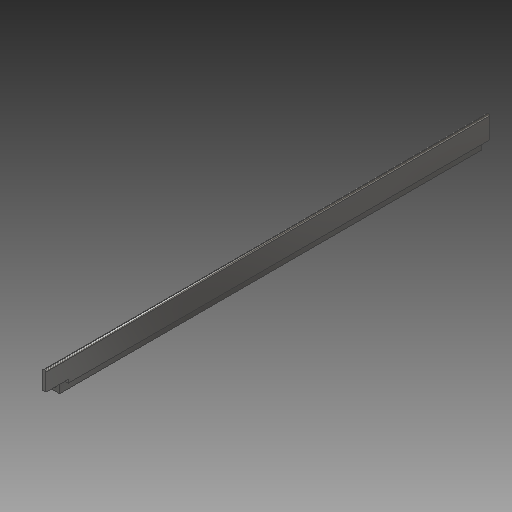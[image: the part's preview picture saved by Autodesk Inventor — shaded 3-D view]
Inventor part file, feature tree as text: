
AUTODESK INVENTOR PART (.ipt)
format: ipt  version: 2019 (Build 230136000, 136)  size: 154,112 bytes
history: native  units: mm
features: plane x4, extrude x2, sketch x2, fillet x1
ambient origin geometry x8: Origin, YZ Plane, XZ Plane, XY Plane, X Axis, Y Axis, Z Axis, Center Point
bodies: Body1 (feature_tree)
feature tree (9):
  extrude  "Extrusion2"  Depth=48.0mm
  plane  "Work Plane4"
  plane  "Work Plane3"
  plane  "Work Plane2"
  plane  "Work Plane1"
  extrude  "Extrusion4"  Depth=32.0mm
  fillet  "Fillet4"  Radius=11.5mm
  sketch  "Sketch1"  dims[d0=20.5mm d1=48.0mm]
  sketch  "Sketch7"  dims[d9=30.0mm d10=32.0mm d11=11.5mm d16=16.0mm d20=600.0mm d21=0.0mm d23=4.5mm d24=4.5mm d25=4.5mm d69=1000.0mm d70=0.0mm d71=30.0mm d73=2.0mm]
